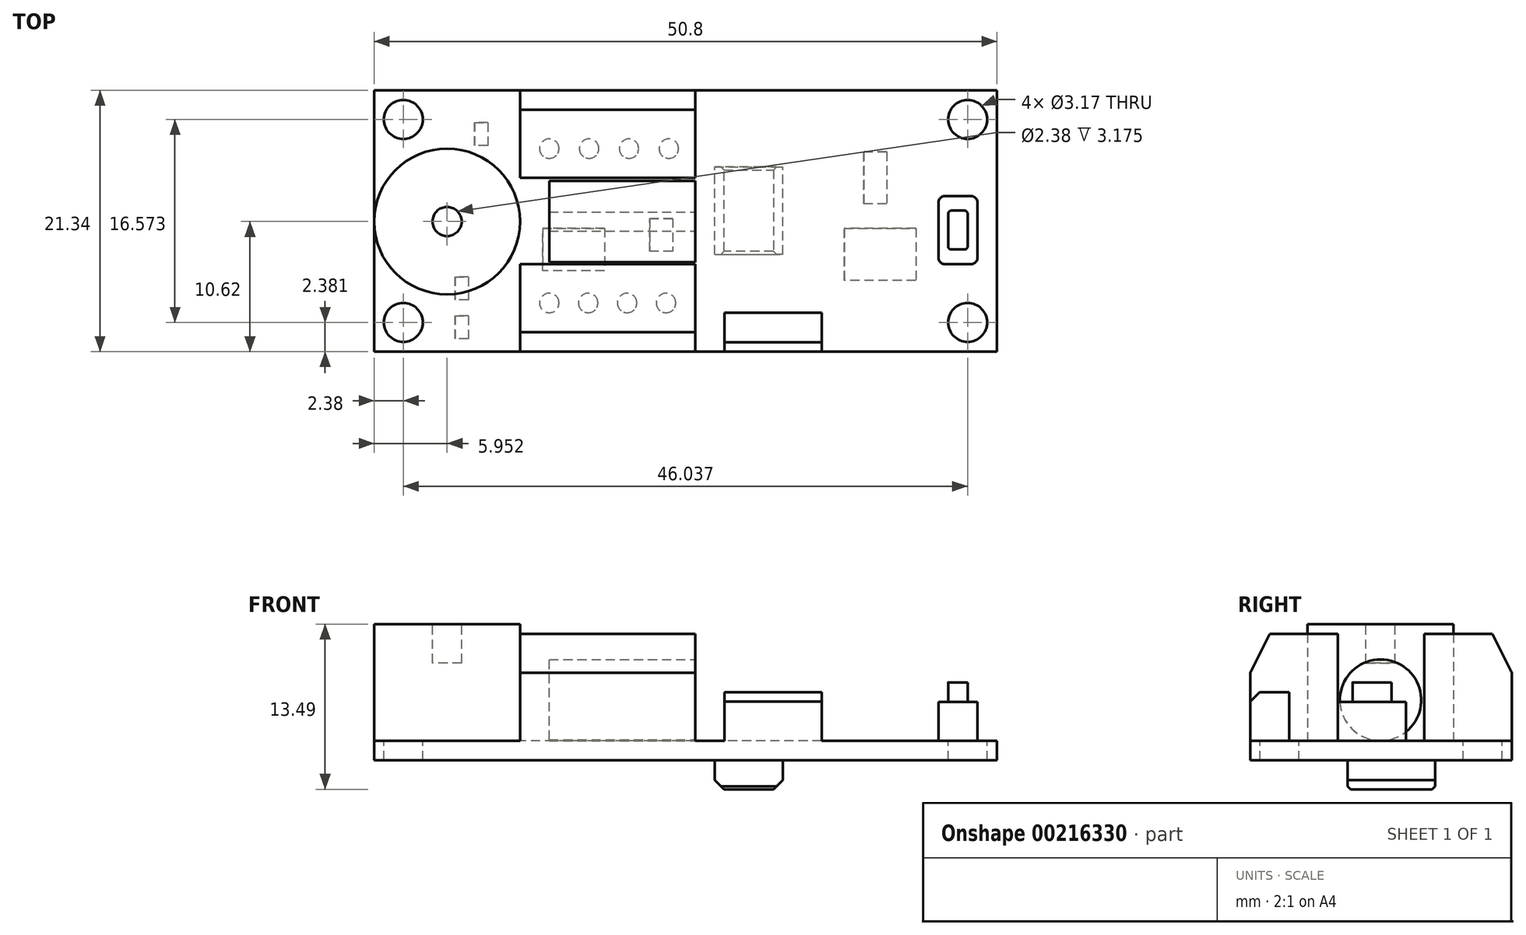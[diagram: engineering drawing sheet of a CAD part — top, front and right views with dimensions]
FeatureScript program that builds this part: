
annotation { "Feature Type Name" : "Feature", "Feature Type Description" : "" }
export const myFeature = defineFeature(function(context is Context, id is Id, definition is map)
    precondition{}
    {
        {
            var Q0;
            Q0=qCreatedBy(makeId("Top.planeOp"),FACE);
            var sketch = newSketch(context, id + "F0", { "sketchPlane" : qUnion([Q0])});
            skLineSegment(sketch, "E0.bottom", {"start": v(-22.64, -9.4) * mm, "end": v(28.16, -9.4) * mm});
            skLineSegment(sketch, "E0.top", {"start": v(-22.64, 11.94) * mm, "end": v(28.16, 11.94) * mm});
            skLineSegment(sketch, "E0.left", {"start": v(-22.64, -9.4) * mm, "end": v(-22.64, 11.94) * mm});
            skLineSegment(sketch, "E0.right", {"start": v(28.16, -9.4) * mm, "end": v(28.16, 11.94) * mm});
            skSolve(sketch);
        }
        {
            var Q0;
            Q0=qSketchRegion(id+"F0",true);
            extrude(context, id + "F1", {"entities" : qUnion([Q0]), "depth" : 1.59 * mm});
        }
        {
            var Q0;
            Q0=makeQuery(id+"F1.opExtrude","CAP_FACE",FACE,{"disambiguationData":[OSD([sQuery(id+"F0.wireOp",EDGE,"E0.bottom"),sQuery(id+"F0.wireOp",EDGE,"E0.top"),sQuery(id+"F0.wireOp",EDGE,"E0.left"),sQuery(id+"F0.wireOp",EDGE,"E0.right")])],"isStart":false});
            var sketch = newSketch(context, id + "F2", { "sketchPlane" : qUnion([Q0])});
            skCircle(sketch, "E1", {"center": v(25.78, -7.02) * mm, "radius": 1.59 * mm});
            skCircle(sketch, "E2", {"center": v(25.78, 9.55) * mm, "radius": 1.59 * mm});
            skCircle(sketch, "E3", {"center": v(-20.26, 9.55) * mm, "radius": 1.59 * mm});
            skCircle(sketch, "E4", {"center": v(-20.26, -7.02) * mm, "radius": 1.59 * mm});
            skSolve(sketch);
        }
        {
            var Q0;
            Q0=qSketchRegion(id+"F2",true);
            extrude(context, id + "F3", {"entities" : qUnion([Q0]), "operationType" : NewBodyOperationType.REMOVE, "oppositeDirection" : true, "depth" : 3.17 * mm});
        }
        {
            var Q0;
            Q0=makeQuery(id+"F1.opExtrude","CAP_FACE",FACE,{"disambiguationData":[OSD([sQuery(id+"F0.wireOp",EDGE,"E0.bottom"),sQuery(id+"F0.wireOp",EDGE,"E0.top"),sQuery(id+"F0.wireOp",EDGE,"E0.left"),sQuery(id+"F0.wireOp",EDGE,"E0.right")])],"isStart":true});
            var sketch = newSketch(context, id + "F4", { "sketchPlane" : qUnion([Q0])});
            skLineSegment(sketch, "E5.bottom", {"start": v(-9.94, -6.38) * mm, "end": v(2.76, -6.38) * mm});
            skLineSegment(sketch, "E5.top", {"start": v(-9.94, -7.97) * mm, "end": v(2.76, -7.97) * mm});
            skLineSegment(sketch, "E5.left", {"start": v(-9.94, -6.38) * mm, "end": v(-9.94, -7.97) * mm});
            skLineSegment(sketch, "E5.right", {"start": v(2.76, -6.38) * mm, "end": v(2.76, -7.97) * mm});
            skLineSegment(sketch, "E6.bottom", {"start": v(-9.94, 4.64) * mm, "end": v(2.76, 4.64) * mm});
            skLineSegment(sketch, "E6.top", {"start": v(-9.94, 6.22) * mm, "end": v(2.76, 6.22) * mm});
            skLineSegment(sketch, "E6.left", {"start": v(-9.94, 4.64) * mm, "end": v(-9.94, 6.22) * mm});
            skLineSegment(sketch, "E6.right", {"start": v(2.76, 4.64) * mm, "end": v(2.76, 6.22) * mm});
            skCircle(sketch, "E7", {"center": v(-8.35, 5.43) * mm, "radius": 0.8 * mm});
            skPoint(sketch, "E7.centerSnap0", {"position": v(-9.94, 5.43) * mm});
            skCircle(sketch, "E8.1.0.0", {"center": v(-5.18, 5.43) * mm, "radius": 0.8 * mm});
            skCircle(sketch, "E8.2.0.0", {"center": v(-2, 5.43) * mm, "radius": 0.8 * mm});
            skCircle(sketch, "E8.3.0.0", {"center": v(1.17, 5.43) * mm, "radius": 0.8 * mm});
            skLineSegment(sketch, "E8.direction1", {"start": v(-8.35, 5.43) * mm, "end": v(-5.18, 5.43) * mm, "construction": true});
            skCircle(sketch, "E9", {"center": v(-8.35, -7.17) * mm, "radius": 0.8 * mm});
            skPoint(sketch, "E9.centerSnap0", {"position": v(-9.94, -7.17) * mm});
            skCircle(sketch, "E10.1.0.0", {"center": v(-5.1, -7.17) * mm, "radius": 0.8 * mm});
            skCircle(sketch, "E10.2.0.0", {"center": v(-1.85, -7.17) * mm, "radius": 0.8 * mm});
            skCircle(sketch, "E10.3.0.0", {"center": v(1.4, -7.17) * mm, "radius": 0.8 * mm});
            skLineSegment(sketch, "E10.direction1", {"start": v(-8.35, -7.17) * mm, "end": v(-5.1, -7.17) * mm, "construction": true});
            skSolve(sketch);
        }
        {
            var Q0;
            {var subQ0=sQuery(id+"F4.wireOp",EDGE,"E8.1.0.0");var subQ1=makeQuery(id+"F4.imprint","INTERSECT",VERTEX,{"derivedFrom":[sQuery(id+"F4.wireOp",EDGE,"E6.bottom"),subQ0]});Q0=makeQuery(id+"F4.imprint","IMPRINT",FACE,{"disambiguationData":[TD([[makeQuery(id+"F4.imprint","IMPRINT",EDGE,{"disambiguationData":[TD([[subQ1,1.0]])],"derivedFrom":subQ0}),1.0]])]});}
            var Q1;
            {var subQ0=sQuery(id+"F4.wireOp",EDGE,"E8.2.0.0");var subQ1=makeQuery(id+"F4.imprint","INTERSECT",VERTEX,{"derivedFrom":[sQuery(id+"F4.wireOp",EDGE,"E6.bottom"),subQ0]});Q1=makeQuery(id+"F4.imprint","IMPRINT",FACE,{"disambiguationData":[TD([[makeQuery(id+"F4.imprint","IMPRINT",EDGE,{"disambiguationData":[TD([[subQ1,1.0]])],"derivedFrom":subQ0}),1.0]])]});}
            var Q2;
            {var subQ0=sQuery(id+"F4.wireOp",EDGE,"E8.3.0.0");var subQ1=makeQuery(id+"F4.imprint","INTERSECT",VERTEX,{"derivedFrom":[sQuery(id+"F4.wireOp",EDGE,"E6.bottom"),subQ0]});Q2=makeQuery(id+"F4.imprint","IMPRINT",FACE,{"disambiguationData":[TD([[makeQuery(id+"F4.imprint","IMPRINT",EDGE,{"disambiguationData":[TD([[subQ1,1.0]])],"derivedFrom":subQ0}),1.0]])]});}
            var Q3;
            {var subQ0=sQuery(id+"F4.wireOp",EDGE,"E9");var subQ1=makeQuery(id+"F4.imprint","INTERSECT",VERTEX,{"derivedFrom":[sQuery(id+"F4.wireOp",EDGE,"E5.bottom"),subQ0]});Q3=makeQuery(id+"F4.imprint","IMPRINT",FACE,{"disambiguationData":[TD([[makeQuery(id+"F4.imprint","IMPRINT",EDGE,{"disambiguationData":[TD([[subQ1,-1.0]])],"derivedFrom":subQ0}),1.0]])]});}
            var Q4;
            {var subQ0=sQuery(id+"F4.wireOp",EDGE,"E10.1.0.0");var subQ1=makeQuery(id+"F4.imprint","INTERSECT",VERTEX,{"derivedFrom":[sQuery(id+"F4.wireOp",EDGE,"E5.bottom"),subQ0]});Q4=makeQuery(id+"F4.imprint","IMPRINT",FACE,{"disambiguationData":[TD([[makeQuery(id+"F4.imprint","IMPRINT",EDGE,{"disambiguationData":[TD([[subQ1,-1.0]])],"derivedFrom":subQ0}),1.0]])]});}
            var Q5;
            {var subQ0=sQuery(id+"F4.wireOp",EDGE,"E10.2.0.0");var subQ1=makeQuery(id+"F4.imprint","INTERSECT",VERTEX,{"derivedFrom":[sQuery(id+"F4.wireOp",EDGE,"E5.bottom"),subQ0]});Q5=makeQuery(id+"F4.imprint","IMPRINT",FACE,{"disambiguationData":[TD([[makeQuery(id+"F4.imprint","IMPRINT",EDGE,{"disambiguationData":[TD([[subQ1,-1.0]])],"derivedFrom":subQ0}),1.0]])]});}
            var Q6;
            {var subQ0=sQuery(id+"F4.wireOp",EDGE,"E10.3.0.0");var subQ1=makeQuery(id+"F4.imprint","INTERSECT",VERTEX,{"derivedFrom":[sQuery(id+"F4.wireOp",EDGE,"E5.bottom"),subQ0]});Q6=makeQuery(id+"F4.imprint","IMPRINT",FACE,{"disambiguationData":[TD([[makeQuery(id+"F4.imprint","IMPRINT",EDGE,{"disambiguationData":[TD([[subQ1,-1.0]])],"derivedFrom":subQ0}),1.0]])]});}
            var Q7;
            {var subQ0=sQuery(id+"F4.wireOp",EDGE,"E7");var subQ1=makeQuery(id+"F4.imprint","INTERSECT",VERTEX,{"derivedFrom":[sQuery(id+"F4.wireOp",EDGE,"E6.bottom"),subQ0]});Q7=makeQuery(id+"F4.imprint","IMPRINT",FACE,{"disambiguationData":[TD([[makeQuery(id+"F4.imprint","IMPRINT",EDGE,{"disambiguationData":[TD([[subQ1,1.0]])],"derivedFrom":subQ0}),1.0]])]});}
            extrude(context, id + "F5", {"entities" : qUnion([Q0, Q1, Q2, Q3, Q4, Q5, Q6, Q7]), "operationType" : NewBodyOperationType.ADD, "depth" : 3 / 812.8 * mm});
        }
        {
            var Q0;
            Q0=makeQuery(id+"F1.opExtrude","CAP_FACE",FACE,{"disambiguationData":[OSD([sQuery(id+"F0.wireOp",EDGE,"E0.bottom"),sQuery(id+"F0.wireOp",EDGE,"E0.top"),sQuery(id+"F0.wireOp",EDGE,"E0.left"),sQuery(id+"F0.wireOp",EDGE,"E0.right")])],"isStart":true});
            var sketch = newSketch(context, id + "F6", { "sketchPlane" : qUnion([Q0])});
            skLineSegment(sketch, "E11.bottom", {"start": v(-16.3, 8.6) * mm, "end": v(-14.7, 8.6) * mm});
            skLineSegment(sketch, "E11.top", {"start": v(-16.3, 6.22) * mm, "end": v(-14.7, 6.22) * mm});
            skLineSegment(sketch, "E11.left", {"start": v(-16.3, 8.6) * mm, "end": v(-16.3, 6.22) * mm});
            skLineSegment(sketch, "E11.right", {"start": v(-14.7, 8.6) * mm, "end": v(-14.7, 6.22) * mm});
            skLineSegment(sketch, "E12.bottom", {"start": v(-16.3, 5.43) * mm, "end": v(-14.7, 5.43) * mm});
            skLineSegment(sketch, "E12.top", {"start": v(-16.3, 3.05) * mm, "end": v(-14.7, 3.05) * mm});
            skLineSegment(sketch, "E12.left", {"start": v(-16.3, 5.43) * mm, "end": v(-16.3, 3.05) * mm});
            skLineSegment(sketch, "E12.right", {"start": v(-14.7, 5.43) * mm, "end": v(-14.7, 3.05) * mm});
            skLineSegment(sketch, "E13.bottom", {"start": v(-14.7, -7.17) * mm, "end": v(-13.12, -7.17) * mm});
            skLineSegment(sketch, "E13.top", {"start": v(-14.7, -9.55) * mm, "end": v(-13.12, -9.55) * mm});
            skLineSegment(sketch, "E13.left", {"start": v(-14.7, -7.17) * mm, "end": v(-14.7, -9.55) * mm});
            skLineSegment(sketch, "E13.right", {"start": v(-13.12, -7.17) * mm, "end": v(-13.12, -9.55) * mm});
            skLineSegment(sketch, "E14.bottom", {"start": v(-9.15, 3.05) * mm, "end": v(-3.6, 3.05) * mm});
            skLineSegment(sketch, "E14.top", {"start": v(-9.15, -0.92) * mm, "end": v(-3.6, -0.92) * mm});
            skLineSegment(sketch, "E14.left", {"start": v(-9.15, 3.05) * mm, "end": v(-9.15, -0.92) * mm});
            skLineSegment(sketch, "E14.right", {"start": v(-3.6, 3.05) * mm, "end": v(-3.6, -0.92) * mm});
            skLineSegment(sketch, "E15.bottom", {"start": v(-0.42, 1.46) * mm, "end": v(1.97, 1.46) * mm});
            skLineSegment(sketch, "E15.top", {"start": v(-0.42, -1.71) * mm, "end": v(1.97, -1.71) * mm});
            skLineSegment(sketch, "E15.left", {"start": v(-0.42, 1.46) * mm, "end": v(-0.42, -1.71) * mm});
            skLineSegment(sketch, "E15.right", {"start": v(1.97, 1.46) * mm, "end": v(1.97, -1.71) * mm});
            skLineSegment(sketch, "E16.bottom", {"start": v(15.46, 3.84) * mm, "end": v(21.8, 3.84) * mm});
            skLineSegment(sketch, "E16.top", {"start": v(15.46, -0.92) * mm, "end": v(21.8, -0.92) * mm});
            skLineSegment(sketch, "E16.left", {"start": v(15.46, 3.84) * mm, "end": v(15.46, -0.92) * mm});
            skLineSegment(sketch, "E16.right", {"start": v(21.8, 3.84) * mm, "end": v(21.8, -0.92) * mm});
            skLineSegment(sketch, "E17.bottom", {"start": v(17.05, -2.41) * mm, "end": v(19.43, -2.41) * mm});
            skLineSegment(sketch, "E17.top", {"start": v(17.05, -7.17) * mm, "end": v(19.43, -7.17) * mm});
            skLineSegment(sketch, "E17.left", {"start": v(17.05, -2.41) * mm, "end": v(17.05, -7.17) * mm});
            skLineSegment(sketch, "E17.right", {"start": v(19.43, -2.41) * mm, "end": v(19.43, -7.17) * mm});
            skSolve(sketch);
        }
        {
            var Q0;
            Q0=qSketchRegion(id+"F6",true);
            extrude(context, id + "F7", {"entities" : qUnion([Q0]), "operationType" : NewBodyOperationType.ADD, "depth" : 1 / 406.4 * mm});
        }
        {
            var Q0;
            Q0=makeQuery(id+"F7.opExtrude","CAP_FACE",FACE,{"disambiguationData":[OSD([sQuery(id+"F6.wireOp",EDGE,"E13.bottom"),sQuery(id+"F6.wireOp",EDGE,"E13.top"),sQuery(id+"F6.wireOp",EDGE,"E13.left"),sQuery(id+"F6.wireOp",EDGE,"E13.right")])],"isStart":false});
            var Q1;
            Q1=makeQuery(id+"F7.opExtrude","CAP_FACE",FACE,{"disambiguationData":[OSD([sQuery(id+"F6.wireOp",EDGE,"E12.bottom"),sQuery(id+"F6.wireOp",EDGE,"E12.top"),sQuery(id+"F6.wireOp",EDGE,"E12.left"),sQuery(id+"F6.wireOp",EDGE,"E12.right")])],"isStart":false});
            var Q2;
            Q2=makeQuery(id+"F7.opExtrude","CAP_FACE",FACE,{"disambiguationData":[OSD([sQuery(id+"F6.wireOp",EDGE,"E11.bottom"),sQuery(id+"F6.wireOp",EDGE,"E11.top"),sQuery(id+"F6.wireOp",EDGE,"E11.left"),sQuery(id+"F6.wireOp",EDGE,"E11.right")])],"isStart":false});
            var Q3;
            Q3=makeQuery(id+"F7.opExtrude","CAP_FACE",FACE,{"disambiguationData":[OSD([sQuery(id+"F6.wireOp",EDGE,"E14.bottom"),sQuery(id+"F6.wireOp",EDGE,"E14.top"),sQuery(id+"F6.wireOp",EDGE,"E14.left"),sQuery(id+"F6.wireOp",EDGE,"E14.right")])],"isStart":false});
            var Q4;
            Q4=makeQuery(id+"F7.opExtrude","CAP_FACE",FACE,{"disambiguationData":[OSD([sQuery(id+"F6.wireOp",EDGE,"E15.bottom"),sQuery(id+"F6.wireOp",EDGE,"E15.top"),sQuery(id+"F6.wireOp",EDGE,"E15.left"),sQuery(id+"F6.wireOp",EDGE,"E15.right")])],"isStart":false});
            var Q5;
            Q5=makeQuery(id+"F7.opExtrude","CAP_FACE",FACE,{"disambiguationData":[OSD([sQuery(id+"F6.wireOp",EDGE,"E16.bottom"),sQuery(id+"F6.wireOp",EDGE,"E16.top"),sQuery(id+"F6.wireOp",EDGE,"E16.left"),sQuery(id+"F6.wireOp",EDGE,"E16.right")])],"isStart":false});
            var Q6;
            Q6=makeQuery(id+"F7.opExtrude","CAP_FACE",FACE,{"disambiguationData":[OSD([sQuery(id+"F6.wireOp",EDGE,"E17.bottom"),sQuery(id+"F6.wireOp",EDGE,"E17.top"),sQuery(id+"F6.wireOp",EDGE,"E17.left"),sQuery(id+"F6.wireOp",EDGE,"E17.right")])],"isStart":false});
            chamfer(context, id + "F8", {"entities" : qUnion([Q0, Q1, Q2, Q3, Q4, Q5, Q6]), "width" : 0.25 * mm, "tangentPropagation" : true});
        }
        {
            var Q0;
            Q0=makeQuery(id+"F1.opExtrude","CAP_FACE",FACE,{"disambiguationData":[OSD([sQuery(id+"F0.wireOp",EDGE,"E0.bottom"),sQuery(id+"F0.wireOp",EDGE,"E0.top"),sQuery(id+"F0.wireOp",EDGE,"E0.left"),sQuery(id+"F0.wireOp",EDGE,"E0.right")])],"isStart":true});
            var sketch = newSketch(context, id + "F9", { "sketchPlane" : qUnion([Q0])});
            skLineSegment(sketch, "E18.bottom", {"start": v(5.14, 1.46) * mm, "end": v(10.7, 1.46) * mm});
            skLineSegment(sketch, "E18.top", {"start": v(5.14, -5.68) * mm, "end": v(10.7, -5.68) * mm});
            skLineSegment(sketch, "E18.left", {"start": v(5.14, 1.46) * mm, "end": v(5.14, -5.68) * mm});
            skLineSegment(sketch, "E18.right", {"start": v(10.7, 1.46) * mm, "end": v(10.7, -5.68) * mm});
            skSolve(sketch);
        }
        {
            var Q0;
            Q0=qSketchRegion(id+"F9",true);
            extrude(context, id + "F10", {"entities" : qUnion([Q0]), "operationType" : NewBodyOperationType.ADD, "depth" : 2.38 * mm});
        }
        {
            var Q0;
            Q0=makeQuery(id+"F10.opExtrude","CAP_EDGE",EDGE,{"disambiguationData":[OSD([sQuery(id+"F9.wireOp",EDGE,"E18.right")])],"isStart":false});
            var Q1;
            Q1=makeQuery(id+"F10.opExtrude","CAP_EDGE",EDGE,{"disambiguationData":[OSD([sQuery(id+"F9.wireOp",EDGE,"E18.left")])],"isStart":false});
            chamfer(context, id + "F11", {"entities" : qUnion([Q0, Q1]), "width" : 0.76 * mm, "tangentPropagation" : true});
        }
        {
            var Q0;
            Q0=makeQuery(id+"F10.opExtrude","CAP_EDGE",EDGE,{"disambiguationData":[OSD([sQuery(id+"F9.wireOp",EDGE,"E18.bottom")])],"isStart":false});
            var Q1;
            Q1=makeQuery(id+"F10.opExtrude","CAP_EDGE",EDGE,{"disambiguationData":[OSD([sQuery(id+"F9.wireOp",EDGE,"E18.top")])],"isStart":false});
            chamfer(context, id + "F12", {"entities" : qUnion([Q0, Q1]), "width" : 0.25 * mm, "tangentPropagation" : true});
        }
        {
            var Q0;
            Q0=makeQuery(id+"F1.opExtrude","CAP_FACE",FACE,{"disambiguationData":[OSD([sQuery(id+"F0.wireOp",EDGE,"E0.bottom"),sQuery(id+"F0.wireOp",EDGE,"E0.top"),sQuery(id+"F0.wireOp",EDGE,"E0.left"),sQuery(id+"F0.wireOp",EDGE,"E0.right")])],"isStart":false});
            var sketch = newSketch(context, id + "F13", { "sketchPlane" : qUnion([Q0])});
            skCircle(sketch, "E19", {"center": v(-16.69, 1.22) * mm, "radius": 5.95 * mm});
            skSolve(sketch);
        }
        {
            var Q0;
            Q0=qSketchRegion(id+"F13",true);
            extrude(context, id + "F14", {"entities" : qUnion([Q0]), "operationType" : NewBodyOperationType.ADD, "depth" : 9.52 * mm});
        }
        {
            var Q0;
            Q0=makeQuery(id+"F14.opExtrude","CAP_FACE",FACE,{"disambiguationData":[OSD([sQuery(id+"F13.wireOp",EDGE,"E19")])],"isStart":false});
            var sketch = newSketch(context, id + "F15", { "sketchPlane" : qUnion([Q0])});
            skCircle(sketch, "E20", {"center": v(-16.69, 1.22) * mm, "radius": 1.2 * mm});
            skSolve(sketch);
        }
        {
            var Q0;
            Q0=qSketchRegion(id+"F15",true);
            extrude(context, id + "F16", {"entities" : qUnion([Q0]), "operationType" : NewBodyOperationType.REMOVE, "oppositeDirection" : true, "depth" : 3.17 * mm});
        }
        {
            var Q0;
            Q0=makeQuery(id+"F1.opExtrude","CAP_FACE",FACE,{"disambiguationData":[OSD([sQuery(id+"F0.wireOp",EDGE,"E0.bottom"),sQuery(id+"F0.wireOp",EDGE,"E0.top"),sQuery(id+"F0.wireOp",EDGE,"E0.left"),sQuery(id+"F0.wireOp",EDGE,"E0.right")])],"isStart":false});
            var sketch = newSketch(context, id + "F17", { "sketchPlane" : qUnion([Q0])});
            skLineSegment(sketch, "E21.bottom", {"start": v(3.55, 4.8) * mm, "end": v(-10.73, 4.8) * mm});
            skLineSegment(sketch, "E21.top", {"start": v(3.55, 11.94) * mm, "end": v(-10.73, 11.94) * mm});
            skLineSegment(sketch, "E21.left", {"start": v(3.55, 4.8) * mm, "end": v(3.55, 11.94) * mm});
            skLineSegment(sketch, "E21.right", {"start": v(-10.73, 4.8) * mm, "end": v(-10.73, 11.94) * mm});
            skLineSegment(sketch, "E22.bottom", {"start": v(3.55, -9.4) * mm, "end": v(-10.73, -9.4) * mm});
            skLineSegment(sketch, "E22.top", {"start": v(3.55, -2.26) * mm, "end": v(-10.73, -2.26) * mm});
            skLineSegment(sketch, "E22.left", {"start": v(3.55, -9.4) * mm, "end": v(3.55, -2.26) * mm});
            skLineSegment(sketch, "E22.right", {"start": v(-10.73, -9.4) * mm, "end": v(-10.73, -2.26) * mm});
            skSolve(sketch);
        }
        {
            var Q0;
            Q0=qSketchRegion(id+"F17",true);
            extrude(context, id + "F18", {"entities" : qUnion([Q0]), "operationType" : NewBodyOperationType.ADD, "depth" : 8.73 * mm});
        }
        {
            var Q0;
            Q0=makeQuery(id+"F18.opExtrude","SWEPT_FACE",FACE,{"disambiguationData":[OSD([sQuery(id+"F17.wireOp",EDGE,"E22.left")])]});
            var sketch = newSketch(context, id + "F19", { "sketchPlane" : qUnion([Q0])});
            skLineSegment(sketch, "E23", {"start": v(-9.4, 7.14) * mm, "end": v(-7.81, 10.32) * mm});
            skLineSegment(sketch, "E24", {"start": v(-7.81, 10.32) * mm, "end": v(-6.85, 13.43) * mm});
            skLineSegment(sketch, "E25", {"start": v(-6.85, 13.43) * mm, "end": v(-12.62, 12.4) * mm});
            skLineSegment(sketch, "E26", {"start": v(-12.62, 12.4) * mm, "end": v(-9.4, 7.14) * mm});
            skLineSegment(sketch, "E27", {"start": v(10.35, 10.32) * mm, "end": v(11.94, 7.14) * mm});
            skLineSegment(sketch, "E28", {"start": v(11.94, 7.14) * mm, "end": v(15.55, 9.64) * mm});
            skLineSegment(sketch, "E29", {"start": v(15.55, 9.64) * mm, "end": v(16.38, 13.68) * mm});
            skLineSegment(sketch, "E30", {"start": v(16.38, 13.68) * mm, "end": v(11.64, 13.16) * mm});
            skLineSegment(sketch, "E31", {"start": v(11.64, 13.16) * mm, "end": v(10.35, 10.32) * mm});
            skSolve(sketch);
        }
        {
            var Q0;
            Q0=qSketchRegion(id+"F19",true);
            extrude(context, id + "F20", {"entities" : qUnion([Q0]), "operationType" : NewBodyOperationType.REMOVE, "oppositeDirection" : true, "depth" : 15.24 * mm});
        }
        {
            var Q0;
            Q0=makeQuery(id+"F18.opExtrude","SWEPT_FACE",FACE,{"disambiguationData":[OSD([sQuery(id+"F17.wireOp",EDGE,"E22.left")])]});
            var sketch = newSketch(context, id + "F21", { "sketchPlane" : qUnion([Q0])});
            skCircle(sketch, "E32", {"center": v(1.22, 4.9) * mm, "radius": 3.32 * mm});
            skLineSegment(sketch, "E33.bottom", {"start": v(0.44, 1.68) * mm, "end": v(2, 1.68) * mm});
            skLineSegment(sketch, "E33.top", {"start": v(0.44, 1.53) * mm, "end": v(2, 1.53) * mm});
            skLineSegment(sketch, "E33.left", {"start": v(0.44, 1.68) * mm, "end": v(0.44, 1.53) * mm});
            skLineSegment(sketch, "E33.right", {"start": v(2, 1.68) * mm, "end": v(2, 1.53) * mm});
            skSolve(sketch);
        }
        {
            var Q0;
            Q0=qSketchRegion(id+"F21",true);
            extrude(context, id + "F22", {"entities" : qUnion([Q0]), "operationType" : NewBodyOperationType.ADD, "oppositeDirection" : true, "depth" : 11.9 * mm});
        }
        {
            var Q0;
            Q0=makeQuery(id+"F1.opExtrude","CAP_FACE",FACE,{"disambiguationData":[OSD([sQuery(id+"F0.wireOp",EDGE,"E0.bottom"),sQuery(id+"F0.wireOp",EDGE,"E0.top"),sQuery(id+"F0.wireOp",EDGE,"E0.left"),sQuery(id+"F0.wireOp",EDGE,"E0.right")])],"isStart":false});
            var sketch = newSketch(context, id + "F23", { "sketchPlane" : qUnion([Q0])});
            skLineSegment(sketch, "E34.bottom", {"start": v(23.4, 3.3) * mm, "end": v(26.57, 3.3) * mm});
            skLineSegment(sketch, "E34.top", {"start": v(23.4, -2.26) * mm, "end": v(26.57, -2.26) * mm});
            skLineSegment(sketch, "E34.left", {"start": v(23.4, 3.3) * mm, "end": v(23.4, -2.26) * mm});
            skLineSegment(sketch, "E34.right", {"start": v(26.57, 3.3) * mm, "end": v(26.57, -2.26) * mm});
            skSolve(sketch);
        }
        {
            var Q0;
            Q0=qSketchRegion(id+"F23",true);
            extrude(context, id + "F24", {"entities" : qUnion([Q0]), "operationType" : NewBodyOperationType.ADD, "depth" : 3.17 * mm});
        }
        {
            var Q0;
            Q0=makeQuery(id+"F24.opExtrude","CAP_FACE",FACE,{"disambiguationData":[OSD([sQuery(id+"F23.wireOp",EDGE,"E34.bottom"),sQuery(id+"F23.wireOp",EDGE,"E34.top"),sQuery(id+"F23.wireOp",EDGE,"E34.left"),sQuery(id+"F23.wireOp",EDGE,"E34.right")])],"isStart":false});
            var sketch = newSketch(context, id + "F25", { "sketchPlane" : qUnion([Q0])});
            skLineSegment(sketch, "E35.bottom", {"start": v(24.2, 2.1) * mm, "end": v(25.78, 2.1) * mm});
            skLineSegment(sketch, "E35.top", {"start": v(24.2, -1.07) * mm, "end": v(25.78, -1.07) * mm});
            skLineSegment(sketch, "E35.left", {"start": v(24.2, 2.1) * mm, "end": v(24.2, -1.07) * mm});
            skLineSegment(sketch, "E35.right", {"start": v(25.78, 2.1) * mm, "end": v(25.78, -1.07) * mm});
            skSolve(sketch);
        }
        {
            var Q0;
            Q0=qSketchRegion(id+"F25",true);
            extrude(context, id + "F26", {"entities" : qUnion([Q0]), "operationType" : NewBodyOperationType.ADD, "depth" : 1.59 * mm});
        }
        {
            var Q0;
            Q0=makeQuery(id+"F26.opExtrude","SWEPT_EDGE",EDGE,{"disambiguationData":[OSD([sQuery(id+"F25.wireOp",EDGE,"E35.top"),sQuery(id+"F25.wireOp",EDGE,"E35.right")])]});
            var Q1;
            Q1=makeQuery(id+"F26.opExtrude","SWEPT_EDGE",EDGE,{"disambiguationData":[OSD([sQuery(id+"F25.wireOp",EDGE,"E35.top"),sQuery(id+"F25.wireOp",EDGE,"E35.left")])]});
            var Q2;
            Q2=makeQuery(id+"F26.opExtrude","SWEPT_EDGE",EDGE,{"disambiguationData":[OSD([sQuery(id+"F25.wireOp",EDGE,"E35.bottom"),sQuery(id+"F25.wireOp",EDGE,"E35.left")])]});
            var Q3;
            Q3=makeQuery(id+"F26.opExtrude","SWEPT_EDGE",EDGE,{"disambiguationData":[OSD([sQuery(id+"F25.wireOp",EDGE,"E35.bottom"),sQuery(id+"F25.wireOp",EDGE,"E35.right")])]});
            fillet(context, id + "F27", {"entities" : qUnion([Q0, Q1, Q2, Q3]), "radius" : 0.25 * mm, "tangentPropagation" : true, "allowEdgeOverflow" : false});
        }
        {
            var Q0;
            Q0=makeQuery(id+"F24.opExtrude","SWEPT_EDGE",EDGE,{"disambiguationData":[OSD([sQuery(id+"F23.wireOp",EDGE,"E34.bottom"),sQuery(id+"F23.wireOp",EDGE,"E34.right")])]});
            var Q1;
            Q1=makeQuery(id+"F24.opExtrude","SWEPT_EDGE",EDGE,{"disambiguationData":[OSD([sQuery(id+"F23.wireOp",EDGE,"E34.bottom"),sQuery(id+"F23.wireOp",EDGE,"E34.left")])]});
            var Q2;
            Q2=makeQuery(id+"F24.opExtrude","SWEPT_EDGE",EDGE,{"disambiguationData":[OSD([sQuery(id+"F23.wireOp",EDGE,"E34.top"),sQuery(id+"F23.wireOp",EDGE,"E34.right")])]});
            var Q3;
            Q3=makeQuery(id+"F24.opExtrude","SWEPT_EDGE",EDGE,{"disambiguationData":[OSD([sQuery(id+"F23.wireOp",EDGE,"E34.top"),sQuery(id+"F23.wireOp",EDGE,"E34.left")])]});
            fillet(context, id + "F28", {"entities" : qUnion([Q0, Q1, Q2, Q3]), "radius" : 0.5 * mm, "tangentPropagation" : true, "allowEdgeOverflow" : false});
        }
        {
            var Q0;
            Q0=makeQuery(id+"F1.opExtrude","CAP_FACE",FACE,{"disambiguationData":[OSD([sQuery(id+"F0.wireOp",EDGE,"E0.bottom"),sQuery(id+"F0.wireOp",EDGE,"E0.top"),sQuery(id+"F0.wireOp",EDGE,"E0.left"),sQuery(id+"F0.wireOp",EDGE,"E0.right")])],"isStart":false});
            var sketch = newSketch(context, id + "F29", { "sketchPlane" : qUnion([Q0])});
            skLineSegment(sketch, "E36.bottom", {"start": v(13.87, -6.22) * mm, "end": v(5.93, -6.22) * mm});
            skLineSegment(sketch, "E36.top", {"start": v(13.87, -9.4) * mm, "end": v(5.93, -9.4) * mm});
            skLineSegment(sketch, "E36.left", {"start": v(13.87, -6.22) * mm, "end": v(13.87, -9.4) * mm});
            skLineSegment(sketch, "E36.right", {"start": v(5.93, -6.22) * mm, "end": v(5.93, -9.4) * mm});
            skSolve(sketch);
        }
        {
            var Q0;
            Q0=qSketchRegion(id+"F29",true);
            extrude(context, id + "F30", {"entities" : qUnion([Q0]), "operationType" : NewBodyOperationType.ADD, "depth" : 3.97 * mm});
        }
        {
            var Q0;
            Q0=makeQuery(id+"F30.opExtrude","CAP_EDGE",EDGE,{"disambiguationData":[OSD([sQuery(id+"F29.wireOp",EDGE,"E36.top")])],"isStart":false});
            chamfer(context, id + "F31", {"entities" : qUnion([Q0]), "width" : 0.76 * mm, "tangentPropagation" : true});
        }
    });
